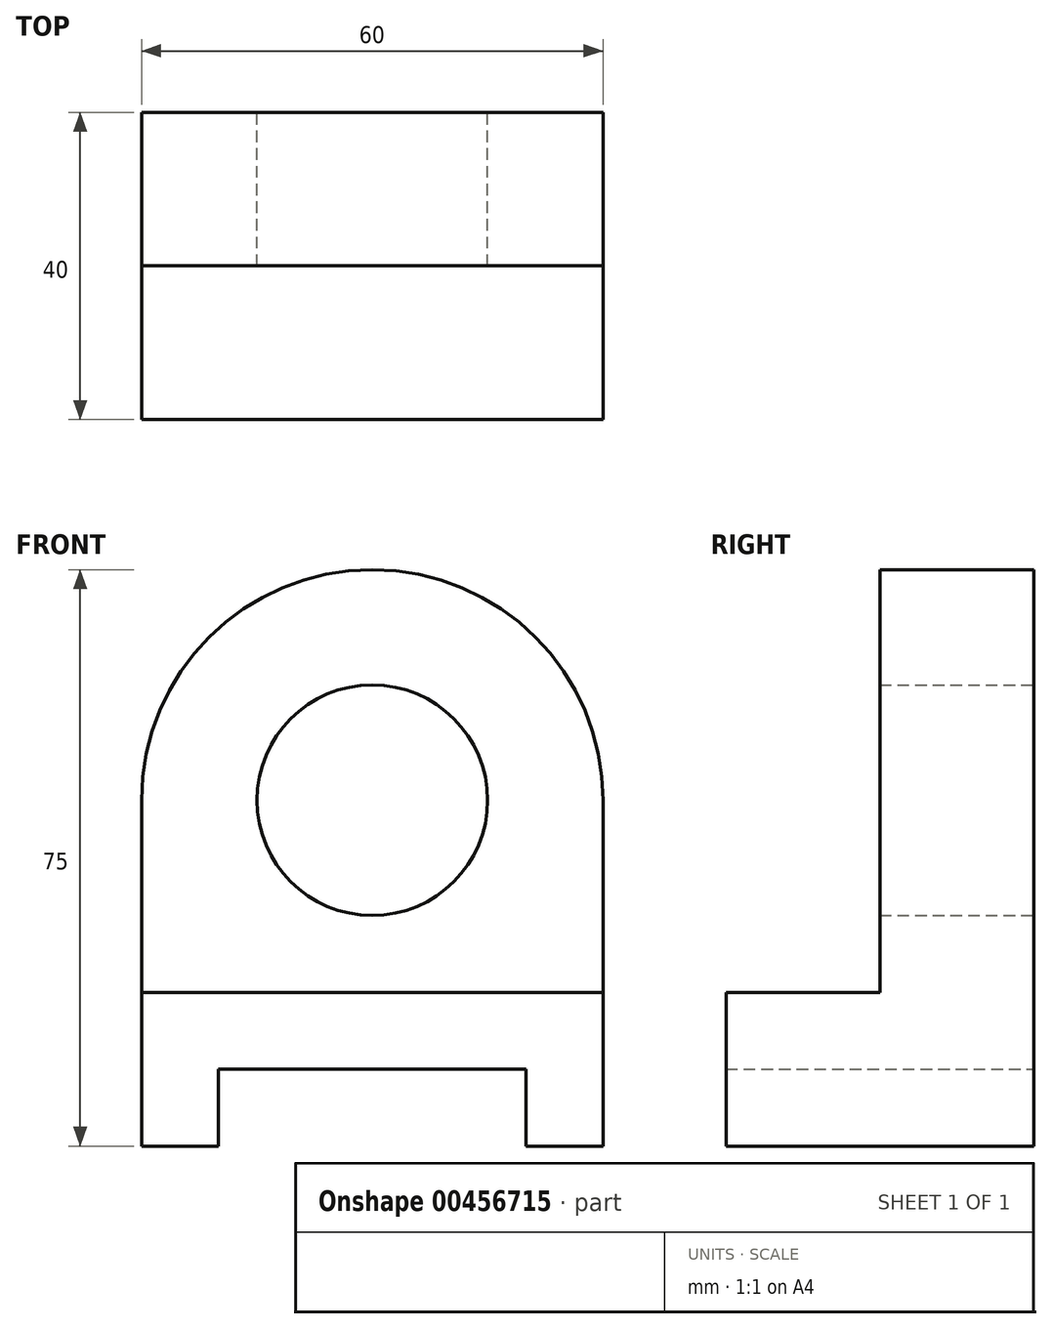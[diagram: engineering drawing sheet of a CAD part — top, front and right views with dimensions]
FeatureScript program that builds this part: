
annotation { "Feature Type Name" : "Feature", "Feature Type Description" : "" }
export const myFeature = defineFeature(function(context is Context, id is Id, definition is map)
    precondition{}
    {
        {
            var Q0;
            Q0=qCreatedBy(makeId("Front.planeOp"),FACE);
            var sketch = newSketch(context, id + "F0", { "sketchPlane" : qUnion([Q0])});
            skLineSegment(sketch, "E0", {"start": v(0, 0) * mm, "end": v(0, 20) * mm});
            skLineSegment(sketch, "E1", {"start": v(0, 20) * mm, "end": v(60, 20) * mm});
            skLineSegment(sketch, "E2", {"start": v(60, 20) * mm, "end": v(60, 0) * mm});
            skLineSegment(sketch, "E3", {"start": v(60, 0) * mm, "end": v(50, 0) * mm});
            skLineSegment(sketch, "E4", {"start": v(50, 0) * mm, "end": v(50, 10) * mm});
            skLineSegment(sketch, "E5", {"start": v(50, 10) * mm, "end": v(10, 10) * mm});
            skLineSegment(sketch, "E6", {"start": v(10, 10) * mm, "end": v(10, 0) * mm});
            skLineSegment(sketch, "E7", {"start": v(10, 0) * mm, "end": v(0, 0) * mm});
            skLineSegment(sketch, "E8", {"start": v(0, 20) * mm, "end": v(0, 45) * mm});
            skLineSegment(sketch, "E9", {"start": v(60, 20) * mm, "end": v(60, 45) * mm});
            skArc(sketch, "E10", {"start": v(60, 45) * mm, "mid": v(30, 75) * mm, "end": v(0, 45) * mm});
            skCircle(sketch, "E11", {"center": v(30, 45) * mm, "radius": 15 * mm});
            skSolve(sketch);
        }
        {
            var Q0;
            Q0=makeQuery(id+"F0.imprint","IMPRINT",FACE,{"disambiguationData":[TD([[makeQuery(id+"F0.imprint","IMPRINT",EDGE,{"derivedFrom":sQuery(id+"F0.wireOp",EDGE,"E0")}),-1.0]])]});
            extrude(context, id + "F1", {"entities" : qUnion([Q0]), "depth" : 40 * mm});
        }
        {
            var Q0;
            Q0=makeQuery(id+"F0.imprint","IMPRINT",FACE,{"disambiguationData":[TD([[makeQuery(id+"F0.imprint","IMPRINT",EDGE,{"derivedFrom":sQuery(id+"F0.wireOp",EDGE,"E1")}),1.0]])]});
            extrude(context, id + "F2", {"entities" : qUnion([Q0]), "operationType" : NewBodyOperationType.ADD, "depth" : 20 * mm});
        }
    });
